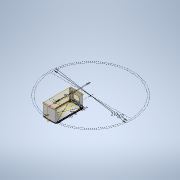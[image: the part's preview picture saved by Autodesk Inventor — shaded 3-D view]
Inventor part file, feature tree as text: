
AUTODESK INVENTOR PART (.ipt)
format: ipt  version: 2020 (Build 240168000, 168)  size: 201,728 bytes
history: native  units: mm
features: projected_geometry x7, sketch x4, extrude x4, other x3
ambient origin geometry x8: Origin, YZ Plane, XZ Plane, XY Plane, X Axis, Y Axis, Z Axis, Center Point
bodies: Body1 (feature_tree)
feature tree (18):
  other  "Твердое тело1"
  sketch  "Эскиз1"
  extrude  "Выдавливание3"  Depth=202.0mm
  other  "РабПлоскость1"
  extrude  "Выдавливание1"  Depth=30.0mm
  other  "РабПлоскость2"
  sketch  "Эскиз2"
  extrude  "Выдавливание4"  Depth=65.0mm
  extrude  "Выдавливание5"  Depth=2.0mm
  sketch  "Эскиз4"
  projected_geometry  "Спроецированная петля1"
  projected_geometry  "Спроецированная петля7"
  projected_geometry  "Спроецированная петля8"
  sketch  "Эскиз3"
  projected_geometry  "Спроецированная петля9"
  projected_geometry  "Спроецированная петля10"
  projected_geometry  "Спроецированная петля11"
  projected_geometry  "Спроецированная петля12"
